# Revit family: Haworth_Typical_Parametric_ComposeBeam_Benching_4Pack
name_source: partatom
category: Furniture Systems
units: mm (PartAtom-declared; Revit-internal decimal feet)

## family parameters
Always vertical = Yes
Cut with Voids When Loaded = No
OmniClass Number = 23.40.70.14.64.21
OmniClass Title = Systems Furniture
Part Type = Normal
Room Calculation Point = No
Round Connector Dimension = Use Diameter
Shared = No
Work Plane-Based = No

## types (4) — shared parameters
Assembly Code = E2020200
Chair Clearance = 42"
Description = Haworth_Typical_Parametric_ComposeBeam_Benching_4Pack
Hardware Finish = Haworth _ Paint _ Undecided _ Panel
Manufacturer = Haworth
Max Length = 84"
Max Worksurface Depth = 29"
Maximum Length = 84 in.
Min Length = 48"
Min Worksurface Depth = 23"
Minimum Length = 48 in.
Model = Haworth_Typical_Parametric_ComposeBeam_Benching_4Pack
Panel Low Tile Finish = Haworth _ Fabric _ Undecided _ Panel
Panel Thickness Half = 1 1/2"
Revision = 1
Screen Finish = Haworth _ Fabric _ Undecided _ Screen
Seat Arm Cap Finish = Haworth _ Polymer _ Undecided
Seat Back Upholstery Finish = Haworth _ Fabric _ Undecided _ Seating _ Task Back
Seat Cushion Finish = Haworth _ Fabric _ Undecided _ Seating _ Task Seat
Seat Shell Finish = Haworth _ Paint _ Undecided _ Seating
Seat Support Finish = Haworth _ Polymer _ Undecided
Size = Verify Final Dim. w/ Haworth
Task Chair = Yes
URL = http://haworth.com
URL - Product = http://haworth.com
With Screen = Yes
Worksurface Finish = Haworth _ Laminate _ Undecided _ Tables

## per-type parameters (varying)
| type | 23in. Surface Depth | 29in. Surface Depth | Actual Spine Length | Actual Spine Length Half | Actual Spine Worksurface Depth | Actual Spine Worksurface Length | Spine Length | Spine Worksurface Depth |
| 72w 30d - 25h Panel, Plus 18h Screen, Chair | No | Yes | 72" | 36" | 31" | 70" | 72" | 29" |
| 84w 30d - 25h Panel, Plus 18h Screen, Chair | No | Yes | 84" | 42" | 31" | 82" | 84" | 29" |
| 60w 24d - 25h Panel, Plus 18h Screen, Chair | Yes | No | 60" | 30" | 25" | 58" | 60" | 23" |
| 48w 24d - 25h Panel, Plus 18h Screen, Chair | Yes | No | 48" | 24" | 25" | 46" | 48" | 23" |

## geometry (parser evidence)
native form markers: Sweep x30
no freeform markers — native parametric forms only
